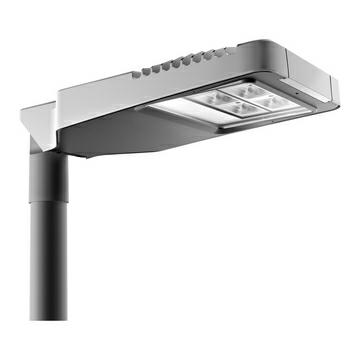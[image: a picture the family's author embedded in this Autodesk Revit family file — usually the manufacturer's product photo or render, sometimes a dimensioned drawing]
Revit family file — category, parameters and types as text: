
# Revit family: Lighting-Stradale-GEWISS-ROAD[5]MINI-LED_OTTICA_CICLOPEDONALE_CLI
name_source: partatom
category: Apparecchi per illuminazione
units: mm (PartAtom-declared; Revit-internal decimal feet)

## family parameters
Basato su piano di lavoro = No
Condiviso = No
Punto di calcolo locali = No
Quota connettore circolare = Usa diametro
Sempre verticale = Sì
Sorgente d'illuminazione = No
Taglio con vuoti quando caricato = No
Tipo di parte = Normale

## types (1)
- Lighting-Stradale-GEWISS-ROAD[5]MINI-LED_OTTICA_CICLOPEDONALE_CLI
    Alimentatore = Incluso
    Apparecchio a ridotta temperatura superficiale = -
    Applicazione = Esterno
    Cablaggio = Sezionatore
    Caratteristiche elettriche e gestione della luce = -
    Caratteristiche ottiche e illuminotecniche = -
    Catalogo = LIGHTING
    Catalogo Serie = ROAD [5]
    Certificazione DIN 18032-3 = -
    Certificazioni e classificazioni = -
    Classe fotobiologica = RG0
    Classe isolamento = I
    Classificazione: = -
    Codice Electrocod = 244C
    Codice digitale univoco (Datamatrix) = Attualmente non presente
    Colore = Grigio grafite
    Contesto = Illuminazione stradale e parcheggi
    Controllo abbagliamento e luminanza = G*3 - ULOR = 0
    Corpo = Alluminio pressofuso
    Corrente di pilotaggio. = 0,7A
    Descrizione = GWR5872M30K - ROAD5 MINI CYCL 2M 3000K 0,7A CL1 1-10V
    Dispositivo di protezione = DM 10KV / CM 10KV
    Distanza minima dall'oggetto illuminato = 1M
    Durata di vita = L90B10 (Tq+25°C) = 100.000 h - L90B10 (Tq+50°C) = 75.000 h
    Efficienza luminosa (lm/W) = 72
    Finitura colore = Verniciato a polveri
    Fissaggio = Testa palo - Sbraccio
    Flusso nominale (lm) = 4090
    Frequenza nominale (Hz) = 50 / 60
    Funzionalità alimentatore = Dimmerabile
    Gancio di chiusura = Maniglia frontale integrata
    Garanzia = 5 anni
    Grado di protezione = IP66
    Gruppo ottico = Riflettore in PC metallizzato
    Guarnizioni = silicone antinvecchiamento
    IDF = 0856e57a-182e-4d26-9af9-9aecbdc27058
    IDT = babf3ceaf7d843279c1ff926cddfbc3c
    IPEA = STRADALE = C // GRANDI AREE = B // CICLOPEDONALI = C // AREE VERDI = C // CENTRO STORICO = A
    Immagine tipo = GWR5276M.jpg
    Inclinazione = -20° ÷ +10° sbraccio - -10° ÷ +20° testa palo
    Indice di resa cromatica = CRI-70
    Informazioni generali = -
    Installazione e manutenzione = -
    LED Life Time (L80B05) = 77000H
    Lampada = LED
    Lampada: = LED
    Lumen output (lm) = 3800
    Materiali = -
    Modello = GWR5872M30K
    Norma di riferimento = EN 60598-2-3, EN 60598-1 IEC/TR 62778
    Numero moduli = 2 (2x3 LED)
    Ottica = CYCLE
    Peso (kg): = 6,59999999999999
    Potenza assorbita : = 53 W @ 0.7A
    Potenza di sistema = 53W
    Produttore = GEWISS S.p.A.
    Regolazione inclinazione = -20° ÷ +10° sbraccio - -10° ÷ +20° testa palo
    Resistenza agli urti = IK08
    Resistenza al filo incandescente = -
    Resistenza alle sovratensioni : = 10 KV in modalità comune e differenziale
    SEO = Stradale
    Scheda Tecnica = https://www.gewiss.com
    Schermo = Vetro piano temperato spessore 4mm
    Sistema di controllo = Dimmerabile 1-10 V
    Sostituibilità gruppo ottico = Non disponibile
    Sostituibilità piastra di cablaggio = Non disponibile
    Superficie massima esposta al vento = 0,149999999999999M2
    Superficie massima esposta al vento : = 0,15 m²
    Temperatura di colore = 3000K
    Temperatura di colore: = 3000 K (CRI>80)
    Temperatura di esercizio = -25 +50 °C
    Temperatura di stoccaggio = -
    Temperatura di utilizzo = -25 +50 °C
    Tensione = 220/240 V - 50/60 Hz - Dimmerabile 1-10 V
    Tensione di alimentazione = 220 - 240 V
    Tipo alimentatore = Driver Led in corrente continua
    Tipo di apparecchio = Apparecchiatura stradale a LED
    Tipo di installazione e montaggio = Testa palo - Sbraccio
    Tipologia = Dimmerabile
    Tipologia sorgente luminosa = LED - Non sostituibile
    Tolleranza cromatica = SDCM = 5
    URL = https://www.gewiss.com
    Vano di alimentazione = Integrato
    Versione file RFA = 20.11
    Viti esterne = Acciaio inox

## geometry (parser evidence)
native form markers: Blend x2
no freeform markers — native parametric forms only
